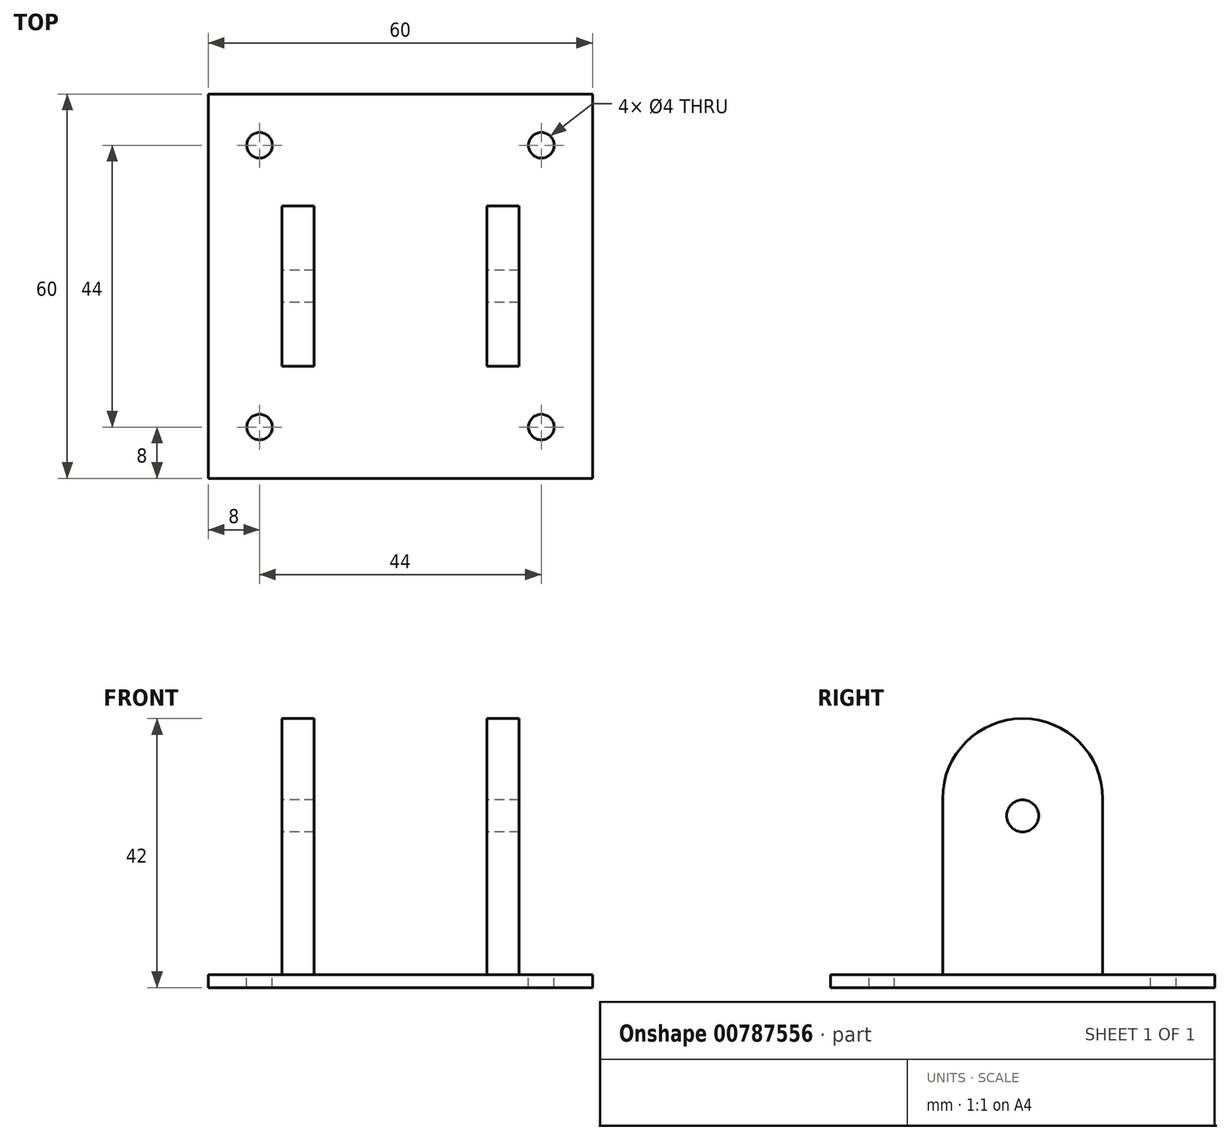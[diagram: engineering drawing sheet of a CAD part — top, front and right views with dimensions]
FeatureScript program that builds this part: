
annotation { "Feature Type Name" : "Feature", "Feature Type Description" : "" }
export const myFeature = defineFeature(function(context is Context, id is Id, definition is map)
    precondition{}
    {
        {
            var Q0;
            Q0=qCreatedBy(makeId("Top.planeOp"),FACE);
            var sketch = newSketch(context, id + "F0", { "sketchPlane" : qUnion([Q0])});
            skLineSegment(sketch, "E0.bottom", {"start": v(5.65, 0) * mm, "end": v(65.65, 0) * mm});
            skLineSegment(sketch, "E0.top", {"start": v(5.65, -60) * mm, "end": v(65.65, -60) * mm});
            skLineSegment(sketch, "E0.left", {"start": v(5.65, 0) * mm, "end": v(5.65, -60) * mm});
            skLineSegment(sketch, "E0.right", {"start": v(65.65, 0) * mm, "end": v(65.65, -60) * mm});
            skSolve(sketch);
        }
        {
            var Q0;
            Q0=makeQuery(id+"F0.imprint","IMPRINT",FACE,{"disambiguationData":[TD([[makeQuery(id+"F0.imprint","IMPRINT",EDGE,{"derivedFrom":sQuery(id+"F0.wireOp",EDGE,"E0.bottom")}),-1.0]])]});
            extrude(context, id + "F1", {"entities" : qUnion([Q0]), "depth" : 2 * mm, "offsetDistance" : 25 * mm});
        }
        {
            var Q0;
            Q0=makeQuery(id+"F1.opExtrude","CAP_FACE",FACE,{"disambiguationData":[OSD([sQuery(id+"F0.wireOp",EDGE,"E0.bottom"),sQuery(id+"F0.wireOp",EDGE,"E0.top"),sQuery(id+"F0.wireOp",EDGE,"E0.left"),sQuery(id+"F0.wireOp",EDGE,"E0.right")])],"isStart":false});
            var sketch = newSketch(context, id + "F2", { "sketchPlane" : qUnion([Q0])});
            skLineSegment(sketch, "E1.bottom", {"start": v(17.15, -17.5) * mm, "end": v(22.15, -17.5) * mm});
            skLineSegment(sketch, "E1.top", {"start": v(17.15, -42.5) * mm, "end": v(22.15, -42.5) * mm});
            skLineSegment(sketch, "E1.left", {"start": v(17.15, -17.5) * mm, "end": v(17.15, -42.5) * mm});
            skLineSegment(sketch, "E1.right", {"start": v(22.15, -17.5) * mm, "end": v(22.15, -42.5) * mm});
            skLineSegment(sketch, "E2.bottom", {"start": v(49.15, -17.5) * mm, "end": v(54.15, -17.5) * mm});
            skLineSegment(sketch, "E2.top", {"start": v(49.15, -42.5) * mm, "end": v(54.15, -42.5) * mm});
            skLineSegment(sketch, "E2.left", {"start": v(49.15, -17.5) * mm, "end": v(49.15, -42.5) * mm});
            skLineSegment(sketch, "E2.right", {"start": v(54.15, -17.5) * mm, "end": v(54.15, -42.5) * mm});
            skSolve(sketch);
        }
        {
            var Q0;
            Q0=makeQuery(id+"F2.imprint","IMPRINT",FACE,{"disambiguationData":[TD([[makeQuery(id+"F2.imprint","IMPRINT",EDGE,{"derivedFrom":sQuery(id+"F2.wireOp",EDGE,"E1.bottom")}),-1.0]])]});
            extrude(context, id + "F3", {"entities" : qUnion([Q0]), "operationType" : NewBodyOperationType.ADD, "depth" : 40 * mm, "offsetDistance" : 25 * mm});
        }
        {
            var Q0;
            Q0=makeQuery(id+"F2.imprint","IMPRINT",FACE,{"disambiguationData":[TD([[makeQuery(id+"F2.imprint","IMPRINT",EDGE,{"derivedFrom":sQuery(id+"F2.wireOp",EDGE,"E2.bottom")}),-1.0]])]});
            extrude(context, id + "F4", {"entities" : qUnion([Q0]), "operationType" : NewBodyOperationType.ADD, "depth" : 40 * mm, "offsetDistance" : 25 * mm});
        }
        {
            var Q0;
            Q0=makeQuery(id+"F3.opExtrude","CAP_EDGE",EDGE,{"disambiguationData":[OSD([sQuery(id+"F2.wireOp",EDGE,"E1.top")])],"isStart":false});
            var Q1;
            Q1=makeQuery(id+"F4.opExtrude","CAP_EDGE",EDGE,{"disambiguationData":[OSD([sQuery(id+"F2.wireOp",EDGE,"E2.top")])],"isStart":false});
            var Q2;
            Q2=makeQuery(id+"F4.opExtrude","CAP_EDGE",EDGE,{"disambiguationData":[OSD([sQuery(id+"F2.wireOp",EDGE,"E2.bottom")])],"isStart":false});
            var Q3;
            Q3=makeQuery(id+"F3.opExtrude","CAP_EDGE",EDGE,{"disambiguationData":[OSD([sQuery(id+"F2.wireOp",EDGE,"E1.bottom")])],"isStart":false});
            fillet(context, id + "F5", {"entities" : qUnion([Q0, Q1, Q2, Q3]), "radius" : 12.5 * mm, "tangentPropagation" : true, "allowEdgeOverflow" : false});
        }
        {
            var Q0;
            Q0=makeQuery(id+"F3.opExtrude","SWEPT_FACE",FACE,{"disambiguationData":[OSD([sQuery(id+"F2.wireOp",EDGE,"E1.left")])]});
            var sketch = newSketch(context, id + "F6", { "sketchPlane" : qUnion([Q0])});
            skCircle(sketch, "E3", {"center": v(30, 26.8) * mm, "radius": 3 * mm});
            skPoint(sketch, "E3.centerSnap0", {"position": v(30, 42) * mm});
            skSolve(sketch);
        }
        {
            var Q0;
            Q0=sQuery(id+"F6.wireOp",VERTEX,"E3.center");
            var Q1;
            Q1=makeQuery(id+"F1.opExtrude","SWEPT_BODY",BODY,{"disambiguationData":[OSD([sQuery(id+"F0.wireOp",EDGE,"E0.bottom"),sQuery(id+"F0.wireOp",EDGE,"E0.top"),sQuery(id+"F0.wireOp",EDGE,"E0.left"),sQuery(id+"F0.wireOp",EDGE,"E0.right")])]});
            hole(context, id + "F7", {"style" : HoleStyle.SIMPLE, "endStyle" : HoleEndStyle.THROUGH, "holeDiameter" : 5 * mm, "majorDiameter" : 5 * mm, "isTappedThrough" : true, "tappedDepth" : 12 * mm, "tapClearance" : 3, "locations" : qUnion([Q0]), "scope" : qUnion([Q1])});
        }
        {
            var Q0;
            Q0=makeQuery(id+"F2.imprint","IMPRINT",FACE,{"disambiguationData":[TD([[makeQuery(id+"F2.imprint","IMPRINT",EDGE,{"derivedFrom":sQuery(id+"F2.wireOp",EDGE,"E1.bottom")}),1.0]])]});
            var sketch = newSketch(context, id + "F8", { "sketchPlane" : qUnion([Q0])});
            skPoint(sketch, "E4", {"position": v(13.65, -8) * mm});
            skPoint(sketch, "E5", {"position": v(57.65, -8) * mm});
            skPoint(sketch, "E6", {"position": v(57.65, -52) * mm});
            skPoint(sketch, "E7", {"position": v(13.65, -52) * mm});
            skSolve(sketch);
        }
        {
            var Q0;
            Q0=sQuery(id+"F8.wireOp",VERTEX,"E4");
            var Q1;
            Q1=sQuery(id+"F8.wireOp",VERTEX,"E7");
            var Q2;
            Q2=sQuery(id+"F8.wireOp",VERTEX,"E6");
            var Q3;
            Q3=sQuery(id+"F8.wireOp",VERTEX,"E5");
            var Q4;
            Q4=makeQuery(id+"F1.opExtrude","SWEPT_BODY",BODY,{"disambiguationData":[OSD([sQuery(id+"F0.wireOp",EDGE,"E0.bottom"),sQuery(id+"F0.wireOp",EDGE,"E0.top"),sQuery(id+"F0.wireOp",EDGE,"E0.left"),sQuery(id+"F0.wireOp",EDGE,"E0.right")])]});
            hole(context, id + "F9", {"style" : HoleStyle.SIMPLE, "endStyle" : HoleEndStyle.BLIND, "holeDiameter" : 4 * mm, "majorDiameter" : 5 * mm, "holeDepth" : 15 * mm, "isTappedThrough" : true, "tappedDepth" : 12 * mm, "tapClearance" : 3, "locations" : qUnion([Q0, Q1, Q2, Q3]), "scope" : qUnion([Q4])});
        }
    });
